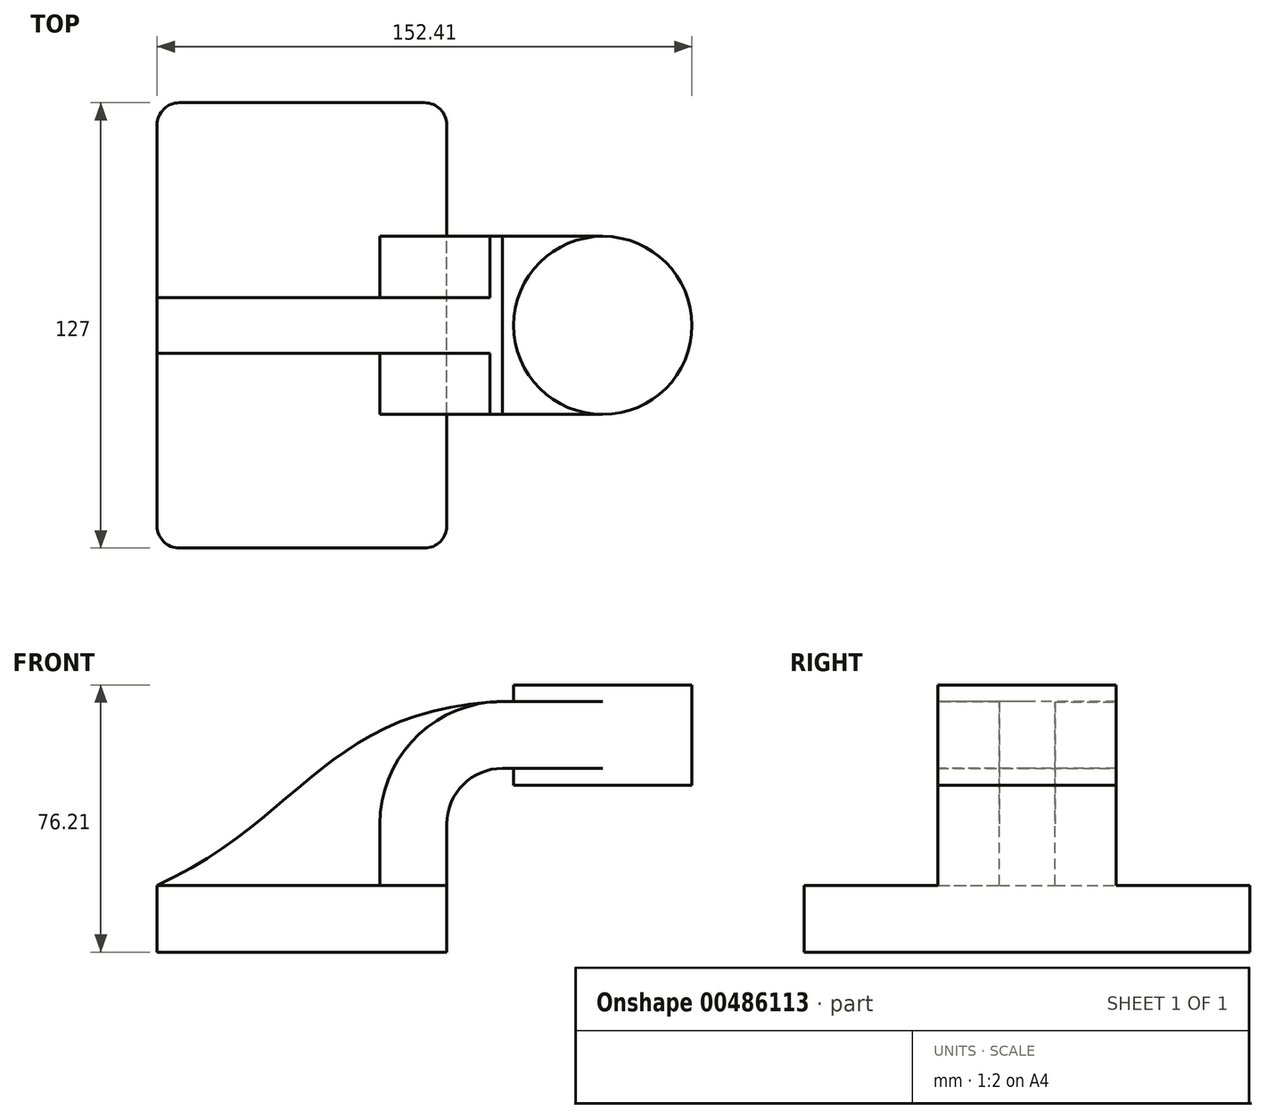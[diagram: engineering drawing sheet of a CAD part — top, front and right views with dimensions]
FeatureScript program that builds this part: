
annotation { "Feature Type Name" : "Feature", "Feature Type Description" : "" }
export const myFeature = defineFeature(function(context is Context, id is Id, definition is map)
    precondition{}
    {
        {
            var Q0;
            Q0=qCreatedBy(makeId("Front.planeOp"),FACE);
            var sketch = newSketch(context, id + "F0", { "sketchPlane" : qUnion([Q0])});
            skLineSegment(sketch, "E0.bottom", {"start": v(-41.28, 9.52) * mm, "end": v(41.28, 9.53) * mm});
            skLineSegment(sketch, "E0.top", {"start": v(-41.28, -9.53) * mm, "end": v(41.28, -9.53) * mm});
            skLineSegment(sketch, "E0.left", {"start": v(-41.28, 9.52) * mm, "end": v(-41.27, -9.53) * mm});
            skLineSegment(sketch, "E0.right", {"start": v(41.28, 9.53) * mm, "end": v(41.28, -9.52) * mm});
            skPoint(sketch, "E0.middle", {"position": v(0, 0) * mm});
            skLineSegment(sketch, "E1.bottom", {"start": v(60.32, 66.68) * mm, "end": v(111.12, 66.68) * mm});
            skLineSegment(sketch, "E1.top", {"start": v(60.32, 38.1) * mm, "end": v(111.12, 38.1) * mm});
            skLineSegment(sketch, "E1.left", {"start": v(60.32, 66.68) * mm, "end": v(60.32, 38.1) * mm});
            skLineSegment(sketch, "E1.right", {"start": v(111.12, 66.68) * mm, "end": v(111.12, 38.1) * mm});
            skPoint(sketch, "E1.middle", {"position": v(85.72, 52.39) * mm});
            skLineSegment(sketch, "E2", {"start": v(41.27, 9.53) * mm, "end": v(41.27, 27) * mm});
            skArc(sketch, "E3", {"start": v(41.27, 27) * mm, "mid": v(45.92, 38.23) * mm, "end": v(57.15, 42.88) * mm});
            skLineSegment(sketch, "E4", {"start": v(57.15, 42.88) * mm, "end": v(85.72, 42.88) * mm});
            skLineSegment(sketch, "E5.0", {"start": v(57.15, 61.93) * mm, "end": v(85.72, 61.93) * mm});
            skArc(sketch, "E5.1", {"start": v(22.22, 27) * mm, "mid": v(32.45, 51.7) * mm, "end": v(57.15, 61.93) * mm});
            skLineSegment(sketch, "E5.2", {"start": v(22.22, 9.53) * mm, "end": v(22.22, 27) * mm});
            skFitSpline(sketch, "E6", {"points": [v(-41.28, 9.52) * mm, v(57.15, 61.93) * mm], "startDerivative": vector(123.83, 56.15) * mm, "endDerivative": vector(149.29, 5.36) * mm});
            skLineSegment(sketch, "E7", {"start": v(85.72, 38.1) * mm, "end": v(85.72, 66.68) * mm});
            skSolve(sketch);
        }
        {
            var Q0;
            Q0=makeQuery(id+"F0.imprint","IMPRINT",FACE,{"disambiguationData":[TD([[makeQuery(id+"F0.imprint","IMPRINT",EDGE,{"derivedFrom":sQuery(id+"F0.wireOp",EDGE,"E0.top")}),1.0]])]});
            extrude(context, id + "F1", {"entities" : qUnion([Q0]), "endBound" : BoundingType.SYMMETRIC, "depth" : 127 * mm});
        }
        {
            var Q0;
            {var subQ1=sQuery(id+"F0.wireOp",EDGE,"E2");Q0=makeQuery(id+"F0.imprint","IMPRINT",FACE,{"disambiguationData":[TD([[makeQuery(id+"F0.imprint","IMPRINT",EDGE,{"derivedFrom":subQ1}),1.0]])]});}
            var Q1;
            {var subQ0=sQuery(id+"F0.wireOp",EDGE,"E5.0");var subQ1=sQuery(id+"F0.wireOp",EDGE,"E1.left");var subQ2=makeQuery(id+"F0.imprint","INTERSECT",VERTEX,{"derivedFrom":[subQ1,subQ0]});Q1=makeQuery(id+"F0.imprint","IMPRINT",FACE,{"disambiguationData":[TD([[makeQuery(id+"F0.imprint","IMPRINT",EDGE,{"disambiguationData":[TD([[subQ2,-1.0]])],"derivedFrom":subQ1}),1.0]])]});}
            extrude(context, id + "F2", {"entities" : qUnion([Q0, Q1]), "operationType" : NewBodyOperationType.ADD, "endBound" : BoundingType.SYMMETRIC, "depth" : 50.8 * mm});
        }
        {
            var Q0;
            {var subQ3=sQuery(id+"F0.wireOp",EDGE,"E5.2");Q0=makeQuery(id+"F0.imprint","IMPRINT",FACE,{"disambiguationData":[TD([[makeQuery(id+"F0.imprint","IMPRINT",EDGE,{"derivedFrom":subQ3}),1.0]])]});}
            extrude(context, id + "F3", {"entities" : qUnion([Q0]), "operationType" : NewBodyOperationType.ADD, "endBound" : BoundingType.SYMMETRIC, "depth" : 15.88 * mm});
        }
        {
            var Q0;
            Q0=makeQuery(id+"F1.opExtrude","CAP_EDGE",EDGE,{"disambiguationData":[OSD([sQuery(id+"F0.wireOp",EDGE,"E0.left")])],"isStart":false});
            var Q1;
            Q1=makeQuery(id+"F1.opExtrude","CAP_EDGE",EDGE,{"disambiguationData":[OSD([sQuery(id+"F0.wireOp",EDGE,"E0.right")])],"isStart":false});
            var Q2;
            Q2=makeQuery(id+"F1.opExtrude","CAP_EDGE",EDGE,{"disambiguationData":[OSD([sQuery(id+"F0.wireOp",EDGE,"E0.right")])],"isStart":true});
            var Q3;
            Q3=makeQuery(id+"F1.opExtrude","CAP_EDGE",EDGE,{"disambiguationData":[OSD([sQuery(id+"F0.wireOp",EDGE,"E0.left")])],"isStart":true});
            fillet(context, id + "F4", {"entities" : qUnion([Q0, Q1, Q2, Q3]), "radius" : 6.35 * mm, "tangentPropagation" : true, "allowEdgeOverflow" : false});
        }
        {
            var Q0;
            {var subQ4=sQuery(id+"F0.wireOp",EDGE,"E1.right");Q0=makeQuery(id+"F0.imprint","IMPRINT",FACE,{"disambiguationData":[TD([[makeQuery(id+"F0.imprint","IMPRINT",EDGE,{"derivedFrom":subQ4}),-1.0]])]});}
            var Q1;
            Q1=sQuery(id+"F0.wireOp",EDGE,"E7");
            revolve(context, id + "F5", {"operationType" : NewBodyOperationType.ADD, "entities" : qUnion([Q0]), "axis" : qUnion([Q1]), "revolveType" : RevolveType.FULL});
        }
    });
